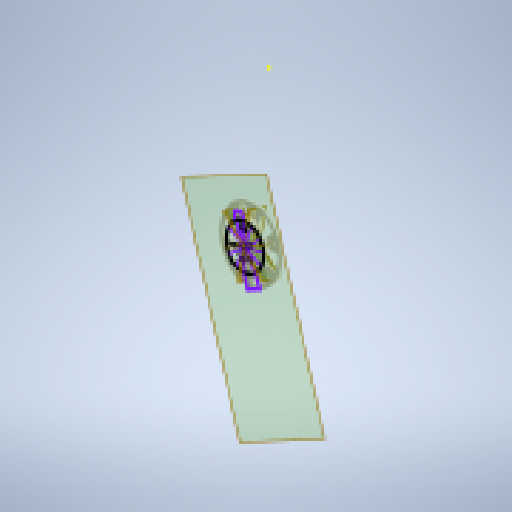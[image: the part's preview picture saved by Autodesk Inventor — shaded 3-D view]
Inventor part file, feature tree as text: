
AUTODESK INVENTOR PART (.ipt)
format: ipt  version: 2023.1 (Build 271208000, 208)  size: 856,576 bytes
history: native  units: in
note: dims shown in document units (in); Inventor stores cm internally (conversion verified against a paired STEP export)
features: plane x7, projected_geometry x6, extrude x5, fillet x4, other x3, sketch x1
ambient origin geometry x8: Origin, YZ Plane, XZ Plane, XY Plane, X Axis, Y Axis, Z Axis, Center Point
bodies: Solid1 (feature_tree)
feature tree (26):
  plane  "Work Plane1"
  sketch  "Sketch1"  dims[d0=2.1654in d1=2.3228in d2=0.0962in d3=0.1575in d4=0.0in d5=0.315in d6=0.0in d27=0.0812in d28=0.0in d29=0.0812in d30=0.0in d31=0.1299in d32=0.1299in d33=0.1299in d34=0.1299in d35=0.1299in d36=0.1299in d37=0.0812in d38=0.0in d39=0.1412in d40=0.0787in d41=0.0394in d42=0.0394in d25=0.0197in d26=0.0344in]
  extrude  "Extrusion1"  Depth=0.0394in
  extrude  "Extrusion2"  Depth=0.0394in
  plane  "Work Plane2"
  plane  "Work Plane3"
  plane  "Work Plane4"
  plane  "Work Plane5"
  plane  "Work Plane6"
  plane  "Work Plane7"
  extrude  "Extrusion7"  Depth=0.0394in TaperAngle=0.0deg
  extrude  "Extrusion8"  Depth=0.0394in TaperAngle=0.0deg
  extrude  "Extrusion9"  Depth=0.0394in TaperAngle=0.0deg
  fillet  "Fillet1"  Radius=0.0812in
  fillet  "Fillet2"  Radius=0.1299in
  fillet  "Fillet3"  Radius=0.1299in
  fillet  "Fillet4"  Radius=0.1299in
  projected_geometry  "Projected Loop1"
  projected_geometry  "Projected Loop2"
  projected_geometry  "Projected Loop3"
  projected_geometry  "Projected Loop4"
  projected_geometry  "Projected Loop5"
  projected_geometry  "Projected Loop6"
  other  "G:\Assembly1.iam"
  other  "Assembly1.iam"
  other  "Plate:1"
